# Revit family: FTTO Power Supply MS700751
name_source: partatom
category: Datengeräte
units: mm (PartAtom-declared; Revit-internal decimal feet)

## family parameters
Arbeitsebenenbasiert = Nein
Beim Laden mit Abzugskörper schneiden = Nein
Bemaßung runder Anschluss = Durchmesser verwenden
Beschriftungsausrichtung beibehalten = Nein
Gemeinsam genutzt = Nein
Immer vertikal = Ja
OmniClass-Nummer = 23.85.50.17
OmniClass-Titel = Communication and Data Processing Equipment
Raumberechnungspunkt = Nein
Teiletyp = Normal

## types (1)
- FTTO Power Supply MS700751
    Artikelnummer = MS700751
    Beschreibung = M45 Micro Power Supply PoE+/++ 150W
    Hersteller = MICROSENS
    Power = 150W
    Property 1 = 1m supply cable
    Property 2 = M45 Design
    Property 3 = Combicon-Plug
    Spannung Input = 115..230VAC
    Spannung Output = 54 VDC/2,8A
    Vorgabe-Ansicht = 0 mm  [stored 0 ft]

note: [stored X ft] marks values corroborated as IEEE doubles in the binary element streams (Revit-internal decimal feet)
